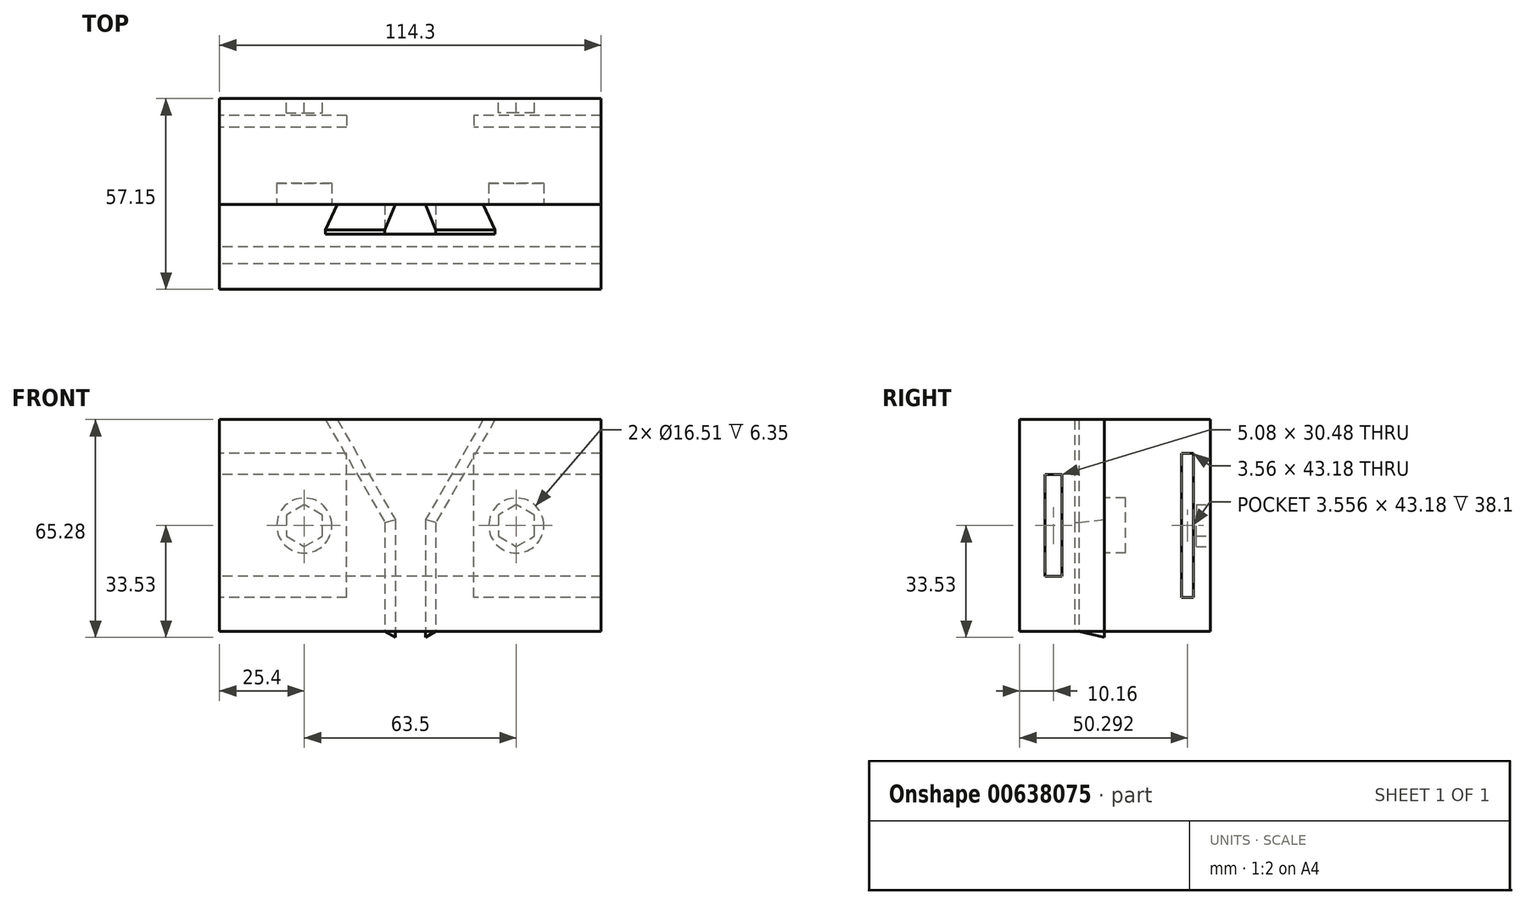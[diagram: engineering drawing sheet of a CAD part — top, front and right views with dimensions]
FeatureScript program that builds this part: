
annotation { "Feature Type Name" : "Feature", "Feature Type Description" : "" }
export const myFeature = defineFeature(function(context is Context, id is Id, definition is map)
    precondition{}
    {
        {
            var Q0;
            Q0=qCreatedBy(makeId("Right.planeOp"),FACE);
            var sketch = newSketch(context, id + "F0", { "sketchPlane" : qUnion([Q0])});
            skLineSegment(sketch, "E0", {"start": v(-26.95, -31.75) * mm, "end": v(36.55, -31.75) * mm});
            skLineSegment(sketch, "E1", {"start": v(36.55, 31.75) * mm, "end": v(-26.95, 31.75) * mm});
            skLineSegment(sketch, "E2", {"start": v(-26.95, 31.75) * mm, "end": v(-26.95, -31.75) * mm});
            skLineSegment(sketch, "E3", {"start": v(-26.95, 19.69) * mm, "end": v(-23.4, 19.69) * mm});
            skLineSegment(sketch, "E4", {"start": v(-23.4, 19.68) * mm, "end": v(-7.9, 8.89) * mm});
            skLineSegment(sketch, "E5", {"start": v(-7.9, 8.9) * mm, "end": v(-7.9, -8.9) * mm});
            skLineSegment(sketch, "E6", {"start": v(-7.9, -8.89) * mm, "end": v(-23.4, -19.68) * mm});
            skLineSegment(sketch, "E7", {"start": v(-23.4, -19.68) * mm, "end": v(-26.95, -19.68) * mm});
            skLineSegment(sketch, "E8.trimOffspring", {"start": v(36.55, -31.75) * mm, "end": v(36.55, 31.75) * mm});
            skLineSegment(sketch, "E9.trimOffspring", {"start": v(4.8, 31.75) * mm, "end": v(4.8, -31.75) * mm});
            skSolve(sketch);
        }
        {
            var Q0;
            {var subQ0=sQuery(id+"F0.wireOp",EDGE,"E8.trimOffspring");Q0=makeQuery(id+"F0.imprint","IMPRINT",FACE,{"disambiguationData":[TD([[makeQuery(id+"F0.imprint","IMPRINT",EDGE,{"derivedFrom":subQ0}),1.0]])]});}
            extrude(context, id + "F1", {"entities" : qUnion([Q0]), "depth" : 114.3 * mm, "offsetDistance" : 25.4 * mm});
        }
        {
            var Q0;
            {var subQ2=sQuery(id+"F0.wireOp",EDGE,"E3");Q0=makeQuery(id+"F0.imprint","IMPRINT",FACE,{"disambiguationData":[TD([[makeQuery(id+"F0.imprint","IMPRINT",EDGE,{"derivedFrom":subQ2}),1.0]])]});}
            var Q1;
            {var subQ0=sQuery(id+"F0.wireOp",EDGE,"E3");Q1=makeQuery(id+"F0.imprint","IMPRINT",FACE,{"disambiguationData":[TD([[makeQuery(id+"F0.imprint","IMPRINT",EDGE,{"derivedFrom":subQ0}),-1.0]])]});}
            extrude(context, id + "F2", {"entities" : qUnion([Q0, Q1]), "depth" : 114.3 * mm, "offsetDistance" : 25.4 * mm});
        }
        {
            var Q0;
            Q0=makeQuery(id+"F2.opExtrude","SWEPT_BODY",BODY,{"disambiguationData":[OSD([sQuery(id+"F0.wireOp",EDGE,"E0"),sQuery(id+"F0.wireOp",EDGE,"E1"),sQuery(id+"F0.wireOp",EDGE,"E2"),sQuery(id+"F0.wireOp",EDGE,"2Nn41NaE-Hgpe-s4fX-lzbf-wooGQdnGQ99G"),sQuery(id+"F0.wireOp",EDGE,"5qlYl4Ai-Fdpj-2xhL-xhdB-RVJ9mpbXSxHZ"),sQuery(id+"F0.wireOp",EDGE,"GVNRazZK-v03o-o9j3-2BiM-VDV5car0XNt5"),sQuery(id+"F0.wireOp",EDGE,"RzVRRZOU-TvBL-98Dw-26rr-Njfk6Q7A123n"),sQuery(id+"F0.wireOp",EDGE,"E9.trimOffspring")])]});
            deleteBodies(context, id + "F3", {"entities" : qUnion([Q0])});
        }
        {
            var Q0;
            Q0=makeQuery(id+"F1.opExtrude","SWEPT_FACE",FACE,{"disambiguationData":[OSD([sQuery(id+"F0.wireOp",EDGE,"E9.trimOffspring")])]});
            var sketch = newSketch(context, id + "F4", { "sketchPlane" : qUnion([Q0])});
            skLineSegment(sketch, "E10", {"start": v(57.15, 31.75) * mm, "end": v(57.15, -31.75) * mm});
            skLineSegment(sketch, "E11.0", {"start": v(31.75, 31.75) * mm, "end": v(49.53, 0.95) * mm});
            skLineSegment(sketch, "E12.0", {"start": v(-6.35, 38.1) * mm, "end": v(-6.35, -38.1) * mm});
            skLineSegment(sketch, "E12.1", {"start": v(120.65, 38.1) * mm, "end": v(-6.35, 38.1) * mm});
            skLineSegment(sketch, "E12.2", {"start": v(120.65, -38.1) * mm, "end": v(120.65, 38.1) * mm});
            skLineSegment(sketch, "E12.3", {"start": v(-6.35, -38.1) * mm, "end": v(120.65, -38.1) * mm});
            skLineSegment(sketch, "E13.0", {"start": v(82.55, 31.75) * mm, "end": v(64.77, 0.95) * mm});
            skLineSegment(sketch, "E14.0", {"start": v(49.53, 0.95) * mm, "end": v(49.53, -31.75) * mm});
            skLineSegment(sketch, "E15.0", {"start": v(64.77, 0.95) * mm, "end": v(64.77, -31.75) * mm});
            skPoint(sketch, "E16.orphan", {"position": v(50.8, -23.24) * mm});
            skSolve(sketch);
        }
        {
            var Q0;
            {var subQ0=sQuery(id+"F0.wireOp",EDGE,"E8.trimOffspring");Q0=makeQuery(id+"F0.imprint","IMPRINT",FACE,{"disambiguationData":[TD([[makeQuery(id+"F0.imprint","IMPRINT",EDGE,{"derivedFrom":subQ0}),1.0]])]});}
            var sketch = newSketch(context, id + "F5", { "sketchPlane" : qUnion([Q0])});
            skLineSegment(sketch, "E17.0", {"start": v(36.55, -31.75) * mm, "end": v(36.55, 31.75) * mm});
            skLineSegment(sketch, "E18.0", {"start": v(31.47, -21.59) * mm, "end": v(31.47, 21.6) * mm});
            skLineSegment(sketch, "E19.0", {"start": v(27.91, -21.59) * mm, "end": v(27.91, 21.6) * mm});
            skPoint(sketch, "E20.orphan", {"position": v(36.55, 0) * mm});
            skLineSegment(sketch, "E21.0", {"start": v(31.47, 21.6) * mm, "end": v(27.91, 21.6) * mm});
            skLineSegment(sketch, "E22.0", {"start": v(31.47, -21.59) * mm, "end": v(27.91, -21.59) * mm});
            skSolve(sketch);
        }
        {
            var Q0;
            Q0=makeQuery(id+"F5.imprint","IMPRINT",FACE,{"disambiguationData":[TD([[makeQuery(id+"F5.imprint","IMPRINT",EDGE,{"derivedFrom":sQuery(id+"F5.wireOp",EDGE,"E18.0")}),1.0]])]});
            extrude(context, id + "F6", {"entities" : qUnion([Q0]), "operationType" : NewBodyOperationType.REMOVE, "depth" : 38.1 * mm, "offsetDistance" : 25.4 * mm});
        }
        {
            var Q0;
            Q0=makeQuery(id+"F5.imprint","IMPRINT",FACE,{"disambiguationData":[TD([[makeQuery(id+"F5.imprint","IMPRINT",EDGE,{"derivedFrom":sQuery(id+"F5.wireOp",EDGE,"E18.0")}),1.0]])]});
            extrude(context, id + "F7", {"entities" : qUnion([Q0]), "operationType" : NewBodyOperationType.REMOVE, "depth" : 114.3 * mm, "offsetDistance" : 25.4 * mm, "hasSecondDirection" : true, "secondDirectionOppositeDirection" : false, "secondDirectionDepth" : 76.2 * mm});
        }
        {
            var Q0;
            {var subQ0=sQuery(id+"F0.wireOp",EDGE,"E1");Q0=makeQuery(id+"Fk5N4uHiYckjh5T_1.boolean.opBoolean","MERGE",FACE,{"derivedFrom":[makeQuery(id+"F1.opExtrude","SWEPT_FACE",FACE,{"disambiguationData":[OSD([subQ0])]}),makeQuery(id+"Fk5N4uHiYckjh5T_1.opExtrude","SWEPT_FACE",FACE,{"disambiguationData":[OSD([subQ0,sQuery(id+"F0.wireOp",EDGE,"E9.trimOffspring")])]})]});}
            var sketch = newSketch(context, id + "F8", { "sketchPlane" : qUnion([Q0])});
            skLineSegment(sketch, "E23", {"start": v(31.75, 4.8) * mm, "end": v(35.3, 4.8) * mm});
            skLineSegment(sketch, "E24", {"start": v(35.3, 4.8) * mm, "end": v(31.75, -2.82) * mm});
            skLineSegment(sketch, "E25", {"start": v(82.55, 4.8) * mm, "end": v(79, 4.8) * mm});
            skLineSegment(sketch, "E26", {"start": v(79, 4.8) * mm, "end": v(82.55, -2.82) * mm});
            skLineSegment(sketch, "E27", {"start": v(31.75, 4.8) * mm, "end": v(31.75, -2.82) * mm});
            skLineSegment(sketch, "E28", {"start": v(82.55, 4.8) * mm, "end": v(82.55, -2.82) * mm});
            skSolve(sketch);
        }
        {
            var Q0;
            Q0=makeQuery(id+"F8.imprint","IMPRINT",FACE,{"disambiguationData":[TD([[makeQuery(id+"F8.imprint","IMPRINT",EDGE,{"derivedFrom":sQuery(id+"F8.wireOp",EDGE,"E23")}),1.0]])]});
            var Q1;
            Q1=sQuery(id+"F4.wireOp",EDGE,"E14.0");
            var Q2;
            Q2=sQuery(id+"F4.wireOp",EDGE,"E11.0");
            sweep(context, id + "F9", {"profiles" : qUnion([Q0]), "path" : qUnion([Q1, Q2])});
        }
        {
            var Q0;
            Q0=makeQuery(id+"F8.imprint","IMPRINT",FACE,{"disambiguationData":[TD([[makeQuery(id+"F8.imprint","IMPRINT",EDGE,{"derivedFrom":sQuery(id+"F8.wireOp",EDGE,"E25")}),1.0]])]});
            var Q1;
            Q1=sQuery(id+"F4.wireOp",EDGE,"E13.0");
            var Q2;
            Q2=sQuery(id+"F4.wireOp",EDGE,"E15.0");
            sweep(context, id + "F10", {"profiles" : qUnion([Q0]), "path" : qUnion([Q1, Q2])});
        }
        {
            var Q0;
            {var subQ0=sQuery(id+"F4.wireOp",EDGE,"E11.0");var subQ2=sQuery(id+"F0.wireOp",EDGE,"E9.trimOffspring");var subQ3=makeQuery(id+"F1.opExtrude","SWEPT_FACE",FACE,{"disambiguationData":[OSD([subQ2])]});Q0=makeQuery(id+"F9.boolean.opBoolean","MERGE",FACE,{"derivedFrom":[makeQuery(id+"Fk5N4uHiYckjh5T_1.boolean.opBoolean","SPLIT",FACE,{"disambiguationData":[TD([makeQuery(id+"Fk5N4uHiYckjh5T_1.opExtrude","SWEPT_FACE",FACE,{"disambiguationData":[OSD([subQ0])]})])],"derivedFrom":subQ3}),makeQuery(id+"F9.opSweep","SWEPT_FACE",FACE,{"disambiguationData":[OSD([subQ0,sQuery(id+"F8.wireOp",EDGE,"E23")])]})]});}
            var sketch = newSketch(context, id + "F11", { "sketchPlane" : qUnion([Q0])});
            skCircle(sketch, "E29", {"center": v(25.4, 0) * mm, "radius": 8.26 * mm});
            skSolve(sketch);
        }
        {
            var Q0;
            {var subQ0=sQuery(id+"F4.wireOp",EDGE,"E13.0");var subQ3=sQuery(id+"F0.wireOp",EDGE,"E9.trimOffspring");var subQ4=makeQuery(id+"F1.opExtrude","SWEPT_FACE",FACE,{"disambiguationData":[OSD([subQ3])]});Q0=makeQuery(id+"F10.boolean.opBoolean","MERGE",FACE,{"derivedFrom":[makeQuery(id+"Fk5N4uHiYckjh5T_1.boolean.opBoolean","SPLIT",FACE,{"disambiguationData":[TD([makeQuery(id+"Fk5N4uHiYckjh5T_1.opExtrude","SWEPT_FACE",FACE,{"disambiguationData":[OSD([subQ0])]})])],"derivedFrom":subQ4}),makeQuery(id+"F10.opSweep","SWEPT_FACE",FACE,{"disambiguationData":[OSD([subQ0,sQuery(id+"F8.wireOp",EDGE,"E25")])]})]});}
            var sketch = newSketch(context, id + "F12", { "sketchPlane" : qUnion([Q0])});
            skCircle(sketch, "E30", {"center": v(88.9, 0) * mm, "radius": 8.26 * mm});
            skSolve(sketch);
        }
        {
            var Q0;
            Q0=makeQuery(id+"F11.imprint","IMPRINT",FACE,{"disambiguationData":[TD([[makeQuery(id+"F11.imprint","IMPRINT",EDGE,{"derivedFrom":sQuery(id+"F11.wireOp",EDGE,"E29")}),1.0]])]});
            var Q1;
            Q1=makeQuery(id+"F12.imprint","IMPRINT",FACE,{"disambiguationData":[TD([[makeQuery(id+"F12.imprint","IMPRINT",EDGE,{"derivedFrom":sQuery(id+"F12.wireOp",EDGE,"E30")}),1.0]])]});
            extrude(context, id + "F13", {"entities" : qUnion([Q0, Q1]), "operationType" : NewBodyOperationType.REMOVE, "oppositeDirection" : true, "depth" : 6.35 * mm, "offsetDistance" : 25.4 * mm});
        }
        {
            var Q0;
            Q0=makeQuery(id+"F1.opExtrude","SWEPT_FACE",FACE,{"disambiguationData":[OSD([sQuery(id+"F0.wireOp",EDGE,"E8.trimOffspring")])]});
            var sketch = newSketch(context, id + "F14", { "sketchPlane" : qUnion([Q0])});
            skCircle(sketch, "E31.cCircle", {"center": v(-88.9, 0) * mm, "radius": 5.44 * mm, "construction": true});
            skLineSegment(sketch, "E31.0", {"start": v(-83.46, 3.14) * mm, "end": v(-83.46, -3.14) * mm});
            skLineSegment(sketch, "E31.1", {"start": v(-83.46, -3.14) * mm, "end": v(-88.9, -6.28) * mm});
            skLineSegment(sketch, "E31.2", {"start": v(-88.9, -6.28) * mm, "end": v(-94.34, -3.14) * mm});
            skLineSegment(sketch, "E31.3", {"start": v(-94.34, -3.14) * mm, "end": v(-94.34, 3.14) * mm});
            skLineSegment(sketch, "E31.4", {"start": v(-94.34, 3.14) * mm, "end": v(-88.9, 6.28) * mm});
            skLineSegment(sketch, "E31.5", {"start": v(-88.9, 6.28) * mm, "end": v(-83.46, 3.14) * mm});
            skPoint(sketch, "E31.0.midPoint", {"position": v(-83.46, 0) * mm});
            skCircle(sketch, "E32.cCircle", {"center": v(-25.4, 0) * mm, "radius": 5.44 * mm, "construction": true});
            skLineSegment(sketch, "E32.0", {"start": v(-30.84, -3.14) * mm, "end": v(-30.84, 3.14) * mm});
            skLineSegment(sketch, "E32.1", {"start": v(-30.84, 3.14) * mm, "end": v(-25.4, 6.28) * mm});
            skLineSegment(sketch, "E32.2", {"start": v(-25.4, 6.28) * mm, "end": v(-19.96, 3.14) * mm});
            skLineSegment(sketch, "E32.3", {"start": v(-19.96, 3.14) * mm, "end": v(-19.96, -3.14) * mm});
            skLineSegment(sketch, "E32.4", {"start": v(-19.96, -3.14) * mm, "end": v(-25.4, -6.28) * mm});
            skLineSegment(sketch, "E32.5", {"start": v(-25.4, -6.28) * mm, "end": v(-30.84, -3.14) * mm});
            skPoint(sketch, "E32.0.midPoint", {"position": v(-30.84, 0) * mm});
            skSolve(sketch);
        }
        {
            var Q0;
            Q0=makeQuery(id+"F14.imprint","IMPRINT",FACE,{"disambiguationData":[TD([[makeQuery(id+"F14.imprint","IMPRINT",EDGE,{"derivedFrom":sQuery(id+"F14.wireOp",EDGE,"E31.0")}),-1.0]])]});
            var Q1;
            Q1=makeQuery(id+"F14.imprint","IMPRINT",FACE,{"disambiguationData":[TD([[makeQuery(id+"F14.imprint","IMPRINT",EDGE,{"derivedFrom":sQuery(id+"F14.wireOp",EDGE,"E32.0")}),-1.0]])]});
            extrude(context, id + "F15", {"entities" : qUnion([Q0, Q1]), "operationType" : NewBodyOperationType.REMOVE, "oppositeDirection" : true, "depth" : 4.27 * mm, "offsetDistance" : 25.4 * mm});
        }
        {
            var Q0;
            {var subQ3=sQuery(id+"F4.wireOp",EDGE,"E11.0");Q0=makeQuery(id+"F4.imprint","IMPRINT",FACE,{"disambiguationData":[TD([[makeQuery(id+"F4.imprint","IMPRINT",EDGE,{"derivedFrom":subQ3}),-1.0]])]});}
            var Q1;
            {var subQ3=sQuery(id+"F4.wireOp",EDGE,"E13.0");Q1=makeQuery(id+"F4.imprint","IMPRINT",FACE,{"disambiguationData":[TD([[makeQuery(id+"F4.imprint","IMPRINT",EDGE,{"derivedFrom":subQ3}),1.0]])]});}
            extrude(context, id + "F16", {"entities" : qUnion([Q0, Q1]), "depth" : 25.4 * mm, "offsetDistance" : 25.4 * mm});
        }
        {
            var Q0;
            {var subQ2=sQuery(id+"F4.wireOp",EDGE,"E10");Q0=makeQuery(id+"F4.imprint","IMPRINT",FACE,{"disambiguationData":[TD([[makeQuery(id+"F4.imprint","IMPRINT",EDGE,{"derivedFrom":subQ2}),-1.0]])]});}
            var Q1;
            {var subQ0=sQuery(id+"F4.wireOp",EDGE,"E10");Q1=makeQuery(id+"F4.imprint","IMPRINT",FACE,{"disambiguationData":[TD([[makeQuery(id+"F4.imprint","IMPRINT",EDGE,{"derivedFrom":subQ0}),1.0]])]});}
            extrude(context, id + "F17", {"entities" : qUnion([Q0, Q1]), "depth" : 25.4 * mm, "offsetDistance" : 25.4 * mm, "hasSecondDirection" : true, "secondDirectionOppositeDirection" : true, "secondDirectionDepth" : -8.9 * mm});
        }
        {
            var Q0;
            Q0=makeQuery(id+"F9.opSweep","SWEPT_BODY",BODY,{"disambiguationData":[OSD([sQuery(id+"F4.wireOp",EDGE,"E11.0"),sQuery(id+"F8.wireOp",EDGE,"E23"),sQuery(id+"F8.wireOp",EDGE,"E24"),sQuery(id+"F8.wireOp",EDGE,"E27")])]});
            var Q1;
            Q1=makeQuery(id+"F10.opSweep","SWEPT_BODY",BODY,{"disambiguationData":[OSD([sQuery(id+"F4.wireOp",EDGE,"E15.0"),sQuery(id+"F8.wireOp",EDGE,"E25"),sQuery(id+"F8.wireOp",EDGE,"E26"),sQuery(id+"F8.wireOp",EDGE,"E28")])]});
            var Q2;
            Q2=makeQuery(id+"F16.opExtrude","SWEPT_BODY",BODY,{"disambiguationData":[OSD([sQuery(id+"F0.wireOp",EDGE,"E0"),sQuery(id+"F0.wireOp",EDGE,"E1"),sQuery(id+"F0.wireOp",EDGE,"E9.trimOffspring"),sQuery(id+"FQNvP4g6ZDJs9w2_2.hole-0.sketch.wireOp",EDGE,"core_line_2"),sQuery(id+"F4.wireOp",EDGE,"E11.0"),sQuery(id+"F4.wireOp",EDGE,"E14.0")])]});
            var Q3;
            Q3=makeQuery(id+"F16.opExtrude","SWEPT_BODY",BODY,{"disambiguationData":[OSD([sQuery(id+"F0.wireOp",EDGE,"E0"),sQuery(id+"F0.wireOp",EDGE,"E1"),sQuery(id+"F0.wireOp",EDGE,"E9.trimOffspring"),sQuery(id+"FQNvP4g6ZDJs9w2_2.hole-1.sketch.wireOp",EDGE,"core_line_2"),sQuery(id+"F4.wireOp",EDGE,"E13.0"),sQuery(id+"F4.wireOp",EDGE,"E15.0")])]});
            var Q4;
            Q4=makeQuery(id+"F17.opExtrude","SWEPT_BODY",BODY,{"disambiguationData":[OSD([sQuery(id+"F0.wireOp",EDGE,"E0"),sQuery(id+"F0.wireOp",EDGE,"E1"),sQuery(id+"F0.wireOp",EDGE,"E9.trimOffspring"),sQuery(id+"F4.wireOp",EDGE,"E11.0"),sQuery(id+"F4.wireOp",EDGE,"E13.0"),sQuery(id+"F4.wireOp",EDGE,"E14.0"),sQuery(id+"F4.wireOp",EDGE,"E15.0")])]});
            booleanBodies(context, id + "F18", {"operationType" : BooleanOperationType.UNION, "tools" : qUnion([Q0, Q1, Q2, Q3, Q4])});
        }
        {
            var Q0;
            {var subQ0=sQuery(id+"F4.wireOp",EDGE,"E15.0");var subQ1=sQuery(id+"F4.wireOp",EDGE,"E14.0");var subQ2=sQuery(id+"F4.wireOp",EDGE,"E13.0");var subQ3=sQuery(id+"F4.wireOp",EDGE,"E11.0");var subQ4=sQuery(id+"F0.wireOp",EDGE,"E9.trimOffspring");var subQ5=sQuery(id+"F0.wireOp",EDGE,"E1");var subQ6=sQuery(id+"F0.wireOp",EDGE,"E0");Q0=makeQuery(id+"F18.opBoolean","MERGE",FACE,{"derivedFrom":[makeQuery(id+"F16.opExtrude","CAP_FACE",FACE,{"disambiguationData":[OSD([subQ6,subQ5,subQ4,sQuery(id+"FQNvP4g6ZDJs9w2_2.hole-0.sketch.wireOp",EDGE,"core_line_2"),subQ3,subQ1])],"isStart":false}),makeQuery(id+"F16.opExtrude","CAP_FACE",FACE,{"disambiguationData":[OSD([subQ6,subQ5,subQ4,sQuery(id+"FQNvP4g6ZDJs9w2_2.hole-1.sketch.wireOp",EDGE,"core_line_2"),subQ2,subQ0])],"isStart":false}),makeQuery(id+"F17.opExtrude","CAP_FACE",FACE,{"disambiguationData":[OSD([subQ6,subQ5,subQ4,subQ3,subQ2,subQ1,subQ0])],"isStart":false})]});}
            var sketch = newSketch(context, id + "F19", { "sketchPlane" : qUnion([Q0])});
            skLineSegment(sketch, "E33.0", {"start": v(114.3, -15.24) * mm, "end": v(0, -15.24) * mm});
            skLineSegment(sketch, "E34.0", {"start": v(114.3, 15.24) * mm, "end": v(0, 15.24) * mm});
            skLineSegment(sketch, "E35", {"start": v(114.3, -15.24) * mm, "end": v(114.3, 15.24) * mm});
            skLineSegment(sketch, "E36", {"start": v(0, -15.24) * mm, "end": v(0, 15.24) * mm});
            skSolve(sketch);
        }
        {
            var Q0;
            Q0=makeQuery(id+"F19.imprint","IMPRINT",FACE,{"disambiguationData":[TD([[makeQuery(id+"F19.imprint","IMPRINT",EDGE,{"derivedFrom":sQuery(id+"F19.wireOp",EDGE,"E33.0")}),-1.0]])]});
            extrude(context, id + "F20", {"entities" : qUnion([Q0]), "operationType" : NewBodyOperationType.REMOVE, "oppositeDirection" : true, "depth" : 12.7 * mm, "offsetDistance" : 25.4 * mm, "hasSecondDirection" : true, "secondDirectionOppositeDirection" : true, "secondDirectionDepth" : 7.62 * mm});
        }
    });
